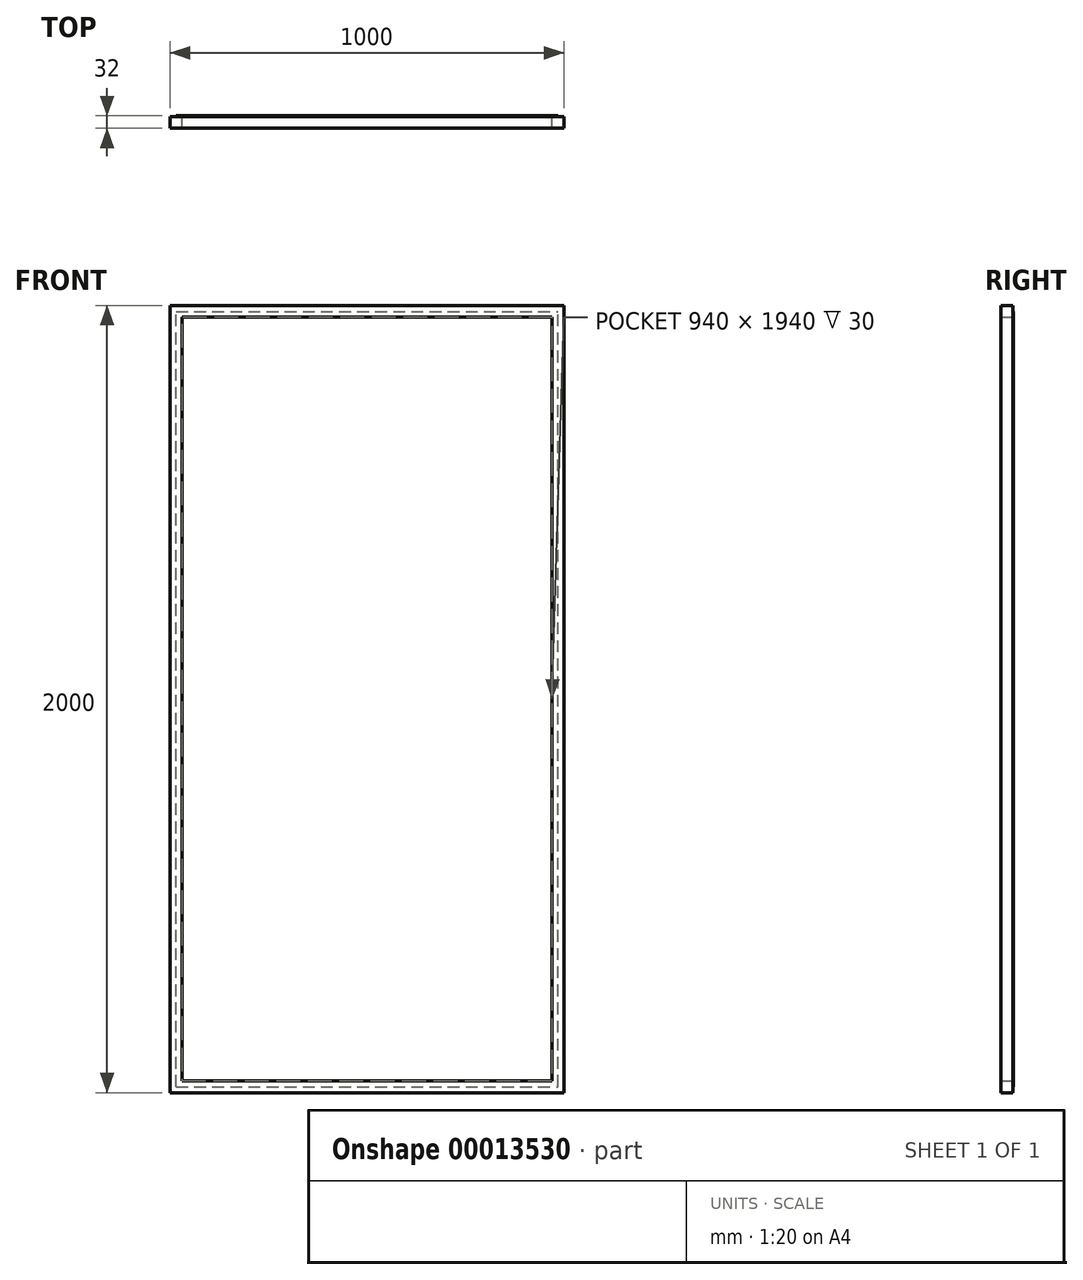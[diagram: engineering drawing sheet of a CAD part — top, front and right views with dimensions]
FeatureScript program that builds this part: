
annotation { "Feature Type Name" : "Feature", "Feature Type Description" : "" }
export const myFeature = defineFeature(function(context is Context, id is Id, definition is map)
    precondition{}
    {
        {
            var Q0;
            Q0=qCreatedBy(makeId("Top.planeOp"),FACE);
            var sketch = newSketch(context, id + "F0", { "sketchPlane" : qUnion([Q0])});
            skLineSegment(sketch, "E0.rect.bottom", {"start": v(-500, 15) * mm, "end": v(500, 15) * mm});
            skLineSegment(sketch, "E0.rect.top", {"start": v(-500, -15) * mm, "end": v(500, -15) * mm});
            skLineSegment(sketch, "E0.rect.left", {"start": v(-500, 15) * mm, "end": v(-500, -15) * mm});
            skLineSegment(sketch, "E0.rect.right", {"start": v(500, 15) * mm, "end": v(500, -15) * mm});
            skPoint(sketch, "E0.rect.middle", {"position": v(0, 0) * mm});
            skSolve(sketch);
        }
        {
            var Q0;
            Q0=qSketchRegion(id+"F0",true);
            extrude(context, id + "F1", {"entities" : qUnion([Q0]), "endBound" : BoundingType.SYMMETRIC, "depth" : 30 * mm});
        }
        {
            var Q0;
            Q0=qCreatedBy(makeId("Front.planeOp"),FACE);
            var sketch = newSketch(context, id + "F2", { "sketchPlane" : qUnion([Q0])});
            skLineSegment(sketch, "E1.bottom", {"start": v(-500, -15) * mm, "end": v(-470, -15) * mm});
            skLineSegment(sketch, "E1.top", {"start": v(-500, -1955) * mm, "end": v(-470, -1955) * mm});
            skLineSegment(sketch, "E1.left", {"start": v(-500, -15) * mm, "end": v(-500, -1955) * mm});
            skLineSegment(sketch, "E1.right", {"start": v(-470, -15) * mm, "end": v(-470, -1955) * mm});
            skLineSegment(sketch, "E2.0.MirrorCS", {"start": v(500, -15) * mm, "end": v(470, -15) * mm});
            skLineSegment(sketch, "E2.1.MirrorCS", {"start": v(500, -1955) * mm, "end": v(470, -1955) * mm});
            skLineSegment(sketch, "E2.2.MirrorCS", {"start": v(500, -15) * mm, "end": v(500, -1955) * mm});
            skLineSegment(sketch, "E2.3.MirrorCS", {"start": v(470, -15) * mm, "end": v(470, -1955) * mm});
            skLineSegment(sketch, "E3.rect.bottom", {"start": v(-500, -1955) * mm, "end": v(500, -1955) * mm});
            skLineSegment(sketch, "E3.rect.top", {"start": v(-500, -1985) * mm, "end": v(500, -1985) * mm});
            skLineSegment(sketch, "E3.rect.left", {"start": v(-500, -1955) * mm, "end": v(-500, -1985) * mm});
            skLineSegment(sketch, "E3.rect.right", {"start": v(500, -1955) * mm, "end": v(500, -1985) * mm});
            skPoint(sketch, "E3.rect.middle", {"position": v(0, -1970) * mm});
            skSolve(sketch);
        }
        {
            var Q0;
            Q0=makeQuery(id+"F2.imprint","IMPRINT",FACE,{"disambiguationData":[TD([[makeQuery(id+"F2.imprint","IMPRINT",EDGE,{"derivedFrom":sQuery(id+"F2.wireOp",EDGE,"E1.bottom")}),-1.0]])]});
            var Q1;
            Q1=makeQuery(id+"F2.imprint","IMPRINT",FACE,{"disambiguationData":[TD([[makeQuery(id+"F2.imprint","IMPRINT",EDGE,{"derivedFrom":sQuery(id+"F2.wireOp",EDGE,"E3.rect.top")}),1.0]])]});
            var Q2;
            Q2=makeQuery(id+"F2.imprint","IMPRINT",FACE,{"disambiguationData":[TD([[makeQuery(id+"F2.imprint","IMPRINT",EDGE,{"derivedFrom":sQuery(id+"F2.wireOp",EDGE,"E2.0.MirrorCS")}),1.0]])]});
            extrude(context, id + "F3", {"entities" : qUnion([Q0, Q1, Q2]), "operationType" : NewBodyOperationType.ADD, "endBound" : BoundingType.SYMMETRIC, "depth" : 30 * mm});
        }
        {
            var Q0;
            Q0=makeQuery(id+"F3.boolean.opBoolean","MERGE",FACE,{"derivedFrom":[makeQuery(id+"F1.opExtrude","SWEPT_FACE",FACE,{"disambiguationData":[OSD([sQuery(id+"F0.wireOp",EDGE,"E0.rect.bottom")])]}),makeQuery(id+"F3.opExtrude","CAP_FACE",FACE,{"disambiguationData":[OSD([sQuery(id+"F2.wireOp",EDGE,"E1.bottom"),sQuery(id+"F2.wireOp",EDGE,"E1.left"),sQuery(id+"F2.wireOp",EDGE,"E1.right"),sQuery(id+"F2.wireOp",EDGE,"E2.0.MirrorCS"),sQuery(id+"F2.wireOp",EDGE,"E2.2.MirrorCS"),sQuery(id+"F2.wireOp",EDGE,"E2.3.MirrorCS"),sQuery(id+"F2.wireOp",EDGE,"E3.rect.bottom"),sQuery(id+"F2.wireOp",EDGE,"E3.rect.top"),sQuery(id+"F2.wireOp",EDGE,"E3.rect.left"),sQuery(id+"F2.wireOp",EDGE,"E3.rect.right")])],"isStart":true})]});
            var sketch = newSketch(context, id + "F4", { "sketchPlane" : qUnion([Q0])});
            skLineSegment(sketch, "E4.bottom", {"start": v(485, -1970) * mm, "end": v(-485, -1970) * mm});
            skLineSegment(sketch, "E4.top", {"start": v(485, 0) * mm, "end": v(-485, 0) * mm});
            skLineSegment(sketch, "E4.left", {"start": v(485, -1970) * mm, "end": v(485, 0) * mm});
            skLineSegment(sketch, "E4.right", {"start": v(-485, -1970) * mm, "end": v(-485, 0) * mm});
            skSolve(sketch);
        }
        {
            var Q0;
            Q0=qSketchRegion(id+"F4",true);
            extrude(context, id + "F5", {"entities" : qUnion([Q0]), "operationType" : NewBodyOperationType.ADD, "depth" : 2 * mm});
        }
    });
